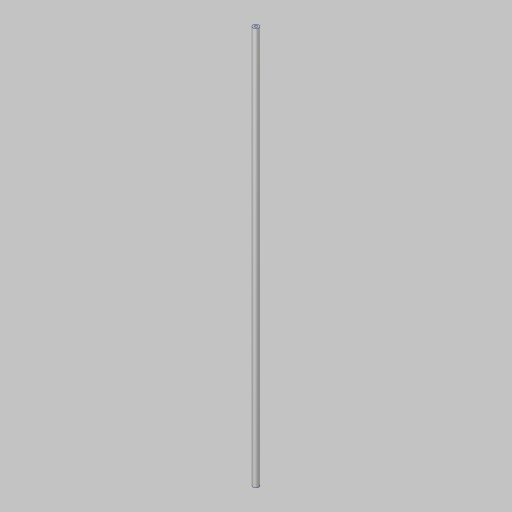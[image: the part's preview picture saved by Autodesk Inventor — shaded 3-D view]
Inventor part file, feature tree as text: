
AUTODESK INVENTOR PART (.ipt)
format: ipt  version: 2023.5 (Build 275446000, 446)  size: 92,672 bytes
history: native  units: in
note: dims shown in document units (in); Inventor stores cm internally (conversion verified against a paired STEP export)
features: sketch x3, hole x2, extrude x1
ambient origin geometry x8: Origin, YZ Plane, XZ Plane, XY Plane, X Axis, Y Axis, Z Axis, Center Point
bodies: Solid1 (feature_tree)
feature tree (6):
  extrude  "Extrusion1"  Depth=33.5in TaperAngle=0.0deg
  hole  "Hole1"  [1 undecoded]
  hole  "Hole2"  [1 undecoded]
  sketch  "Sketch1"  dims[d0=0.5in d1=33.5in d2=0.0in]
  sketch  "Sketch2"  dims[d3=0.196in d4=0.5in d5=0.507in d6=0.25in d7=0.5635in d8=0.75in d9=0.8108in]
  sketch  "Sketch3"  dims[d10=0.196in d11=0.5in d12=0.375in d13=0.25in d14=0.5635in d15=1.5in d16=0.8108in]
note: 2 required parameter values undecoded (feature->parameter linkage not recoverable at this tier; creation-order binding heuristic only, values carry confidence <= 0.55)
